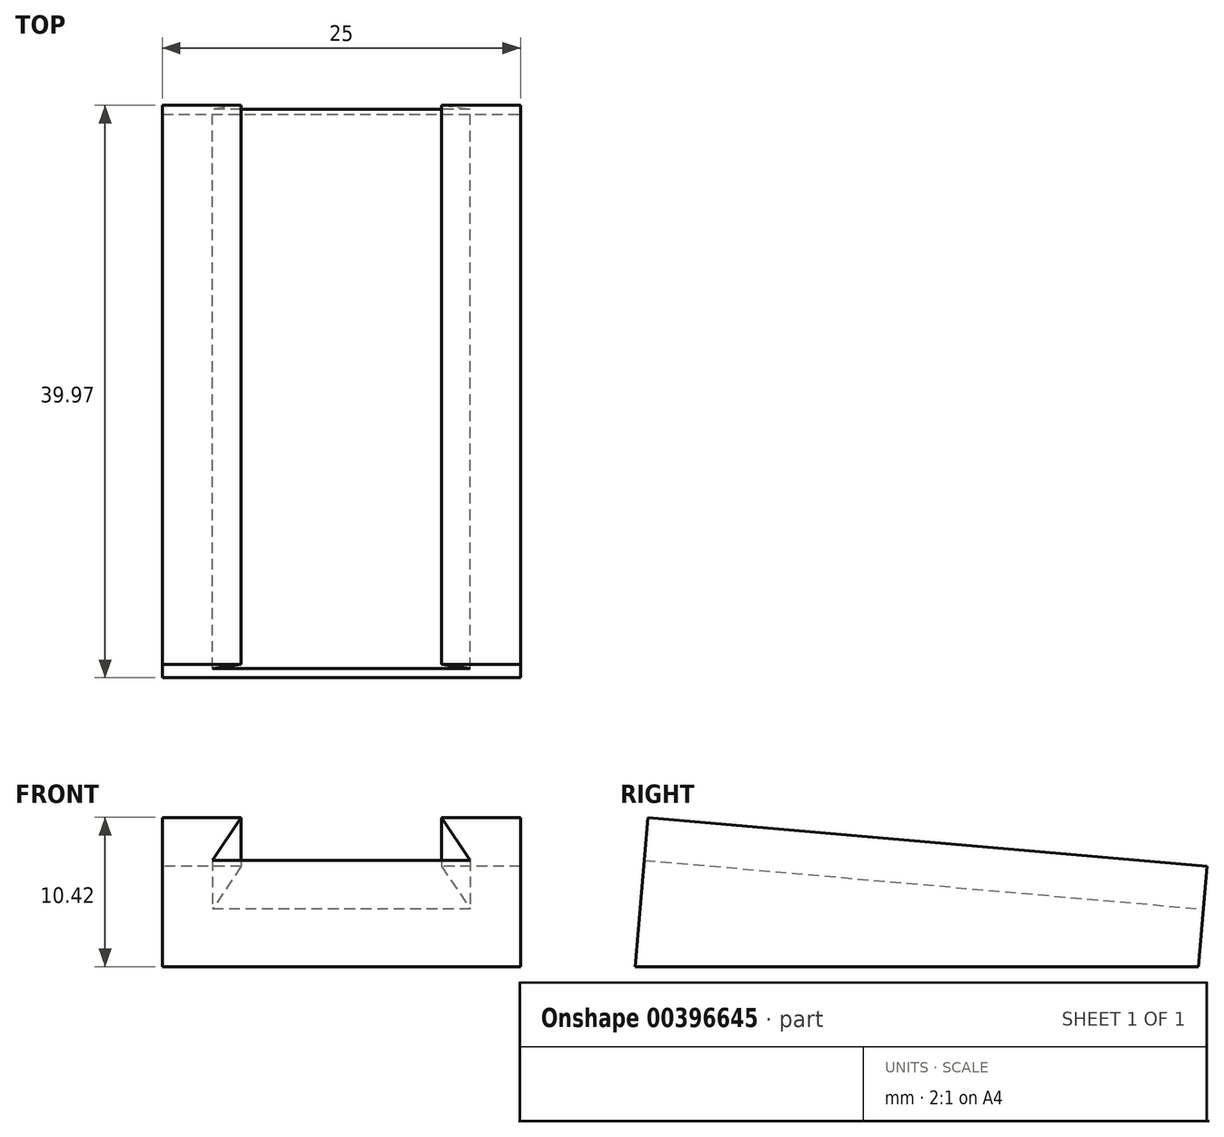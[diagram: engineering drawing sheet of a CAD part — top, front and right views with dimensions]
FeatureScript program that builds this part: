
annotation { "Feature Type Name" : "Feature", "Feature Type Description" : "" }
export const myFeature = defineFeature(function(context is Context, id is Id, definition is map)
    precondition{}
    {
        {
            assignVariable(context, id + "F0", {"name" : "baseWidth", "anyValue" : 25});
        }
        {
            var Q0;
            Q0=qCreatedBy(makeId("Right.planeOp"),FACE);
            var sketch = newSketch(context, id + "F1", { "sketchPlane" : qUnion([Q0])});
            skLineSegment(sketch, "E0.top", {"start": v(20, 0) * mm, "end": v(-20, 0) * mm});
            skLineSegment(sketch, "E0.left", {"start": v(20, 7) * mm, "end": v(20, 0) * mm});
            skLineSegment(sketch, "E0.right", {"start": v(-20, 7) * mm, "end": v(-20, 0) * mm});
            skLineSegment(sketch, "E1", {"start": v(-20, 7) * mm, "end": v(-20, 10.5) * mm});
            skLineSegment(sketch, "E2", {"start": v(-20, 10.5) * mm, "end": v(20, 7) * mm});
            skSolve(sketch);
        }
        {
            var Q0;
            Q0=makeQuery(id+"F1.imprint","IMPRINT",FACE,{"disambiguationData":[TD([[makeQuery(id+"F1.imprint","IMPRINT",EDGE,{"derivedFrom":sQuery(id+"F1.wireOp",EDGE,"E0.top")}),-1.0]])]});
            extrude(context, id + "F2", {"entities" : qUnion([Q0]), "endBound" : BoundingType.SYMMETRIC, "depth" : (getVariable(context, 'baseWidth')) * mm});
        }
        {
            var Q0;
            Q0=makeQuery(id+"F2.opExtrude","SWEPT_FACE",FACE,{"disambiguationData":[OSD([sQuery(id+"F1.wireOp",EDGE,"E2")])]});
            var sketch = newSketch(context, id + "F3", { "sketchPlane" : qUnion([Q0])});
            skLineSegment(sketch, "E3.bottom", {"start": v(12.5, -20.84) * mm, "end": v(-12.5, -20.84) * mm});
            skLineSegment(sketch, "E3.top", {"start": v(12.5, -28.39) * mm, "end": v(-12.5, -28.39) * mm});
            skLineSegment(sketch, "E3.left", {"start": v(12.5, -20.84) * mm, "end": v(12.5, -28.39) * mm});
            skLineSegment(sketch, "E3.right", {"start": v(-12.5, -20.84) * mm, "end": v(-12.5, -28.39) * mm});
            skSolve(sketch);
        }
        {
            var Q0;
            Q0=makeQuery(id+"F3.imprint","IMPRINT",FACE,{"disambiguationData":[TD([[makeQuery(id+"F3.imprint","IMPRINT",EDGE,{"derivedFrom":sQuery(id+"F3.wireOp",EDGE,"E3.bottom")}),1.0]])]});
            extrude(context, id + "F4", {"entities" : qUnion([Q0]), "endBound" : BoundingType.SYMMETRIC, "depth" : 25 * mm});
        }
        {
            var Q0;
            Q0=makeQuery(id+"F4.opExtrude","SWEPT_FACE",FACE,{"disambiguationData":[OSD([sQuery(id+"F3.wireOp",EDGE,"E3.bottom")])]});
            cPlane(context, id + "F5", {"entities" : qUnion([Q0]), "cplaneType" : CPlaneType.OFFSET, "offset" : 40.15 * mm, "width" : 150 * mm, "height" : 150 * mm});
        }
        {
            var Q0;
            Q0=qCreatedBy(id+"F5.planeOp",FACE);
            var sketch = newSketch(context, id + "F6", { "sketchPlane" : qUnion([Q0])});
            skLineSegment(sketch, "E4.bottom", {"start": v(7, 5.72) * mm, "end": v(-7, 5.72) * mm});
            skLineSegment(sketch, "E4.top", {"start": v(7, 8.72) * mm, "end": v(-7, 8.72) * mm});
            skLineSegment(sketch, "E5", {"start": v(-7, 8.72) * mm, "end": v(-9, 5.72) * mm});
            skLineSegment(sketch, "E6", {"start": v(-9, 5.72) * mm, "end": v(-7, 5.72) * mm});
            skLineSegment(sketch, "E7", {"start": v(7, 8.72) * mm, "end": v(9, 5.72) * mm});
            skLineSegment(sketch, "E8", {"start": v(9, 5.72) * mm, "end": v(7, 5.72) * mm});
            skLineSegment(sketch, "E9", {"start": v(-7, 8.72) * mm, "end": v(7, 8.72) * mm});
            skLineSegment(sketch, "E10", {"start": v(0, 1.78) * mm, "end": v(0, 5.72) * mm, "construction": true});
            skSolve(sketch);
        }
        {
            var Q0;
            Q0 = qSketchRegion(id + "F6", true);
            extrude(context, id + "F7", {"entities" : qUnion([Q0]), "operationType" : NewBodyOperationType.REMOVE, "endBound" : BoundingType.THROUGH_ALL, "oppositeDirection" : true, "depth" : 25 * mm, "hasSecondDirection" : true, "secondDirectionBound" : SecondDirectionBoundingType.THROUGH_ALL, "secondDirectionOppositeDirection" : false, "secondDirectionDepth" : 25 * mm});
        }
        {
            var Q0;
            Q0=makeQuery(id+"F4.opExtrude","SWEPT_FACE",FACE,{"disambiguationData":[OSD([sQuery(id+"F3.wireOp",EDGE,"E3.top")])]});
            var Q1;
            Q1=makeQuery(id+"F4.opExtrude","SWEPT_FACE",FACE,{"disambiguationData":[OSD([sQuery(id+"F3.wireOp",EDGE,"E3.bottom")])]});
            extrude(context, id + "F8", {"entities" : qUnion([Q0]), "operationType" : NewBodyOperationType.REMOVE, "endBound" : BoundingType.UP_TO_SURFACE, "oppositeDirection" : true, "endBoundEntityFace" : qUnion([Q1]), "depth" : 25 * mm});
        }
        {
            var Q0;
            Q0=qCreatedBy(id+"F5.planeOp",FACE);
            cPlane(context, id + "F9", {"entities" : qUnion([Q0]), "cplaneType" : CPlaneType.OFFSET, "offset" : 39.2 * mm, "oppositeDirection" : true, "width" : 150 * mm, "height" : 150 * mm});
        }
        {
            var Q0;
            Q0=makeQuery(id+"F2.opExtrude","CAP_FACE",FACE,{"disambiguationData":[OSD([sQuery(id+"F1.wireOp",EDGE,"E0.top"),sQuery(id+"F1.wireOp",EDGE,"E0.left"),sQuery(id+"F1.wireOp",EDGE,"E0.right"),sQuery(id+"F1.wireOp",EDGE,"E1"),sQuery(id+"F1.wireOp",EDGE,"E2")])],"isStart":false});
            var sketch = newSketch(context, id + "F10", { "sketchPlane" : qUnion([Q0])});
            skLineSegment(sketch, "E11", {"start": v(20, 7) * mm, "end": v(19.39, 0) * mm});
            skLineSegment(sketch, "E12", {"start": v(19.39, 0) * mm, "end": v(20, 0) * mm});
            skLineSegment(sketch, "E13", {"start": v(20, 0) * mm, "end": v(20, 7) * mm});
            skPoint(sketch, "E14", {"position": v(-19.97, 0) * mm});
            skLineSegment(sketch, "E15", {"start": v(-19.97, 0) * mm, "end": v(-20, 0) * mm});
            skLineSegment(sketch, "E16", {"start": v(-20, 0) * mm, "end": v(-20, 10.5) * mm});
            skPoint(sketch, "E17", {"position": v(-19.05, 10.42) * mm});
            skLineSegment(sketch, "E18", {"start": v(-20, 10.5) * mm, "end": v(-19.05, 10.42) * mm});
            skLineSegment(sketch, "E19", {"start": v(-19.05, 10.42) * mm, "end": v(-19.97, 0) * mm});
            skSolve(sketch);
        }
        {
            var Q0;
            Q0=makeQuery(id+"F10.imprint","IMPRINT",FACE,{"disambiguationData":[TD([[makeQuery(id+"F10.imprint","IMPRINT",EDGE,{"derivedFrom":sQuery(id+"F10.wireOp",EDGE,"E15")}),-1.0]])]});
            var Q1;
            Q1=makeQuery(id+"F10.imprint","IMPRINT",FACE,{"disambiguationData":[TD([[makeQuery(id+"F10.imprint","IMPRINT",EDGE,{"derivedFrom":sQuery(id+"F10.wireOp",EDGE,"E11")}),1.0]])]});
            var Q2;
            Q2=makeQuery(id+"F2.opExtrude","CAP_FACE",FACE,{"disambiguationData":[OSD([sQuery(id+"F1.wireOp",EDGE,"E0.top"),sQuery(id+"F1.wireOp",EDGE,"E0.left"),sQuery(id+"F1.wireOp",EDGE,"E0.right"),sQuery(id+"F1.wireOp",EDGE,"E1"),sQuery(id+"F1.wireOp",EDGE,"E2")])],"isStart":true});
            extrude(context, id + "F11", {"entities" : qUnion([Q0, Q1]), "operationType" : NewBodyOperationType.REMOVE, "endBound" : BoundingType.UP_TO_SURFACE, "oppositeDirection" : true, "endBoundEntityFace" : qUnion([Q2]), "depth" : 25 * mm});
        }
    });
